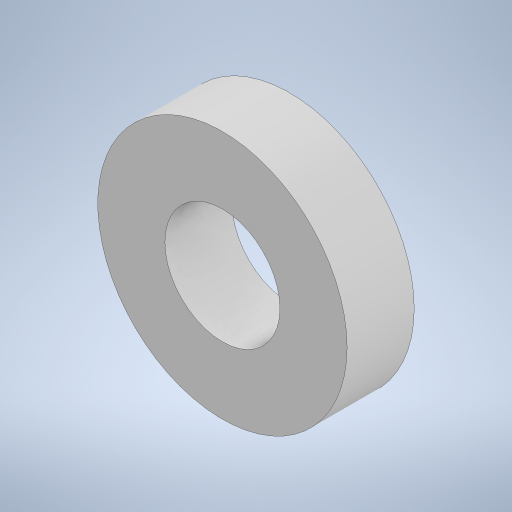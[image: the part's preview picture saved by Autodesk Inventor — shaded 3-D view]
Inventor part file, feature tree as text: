
AUTODESK INVENTOR PART (.ipt)
format: ipt  version: 2023 (Build 270158000, 158)  size: 214,528 bytes
history: native  units: in
note: dims shown in document units (in); Inventor stores cm internally (conversion verified against a paired STEP export)
features: extrude x1, sketch x1
ambient origin geometry x8: Origin, YZ Plane, XZ Plane, XY Plane, X Axis, Y Axis, Z Axis, Center Point
bodies: Solid1 (feature_tree)
feature tree (2):
  extrude  "Extrusion1"  Depth=0.4375in
  sketch  "Sketch1"  dims[d0=0.75in d1=1.625in d2=0.4375in d3=0.0in]
